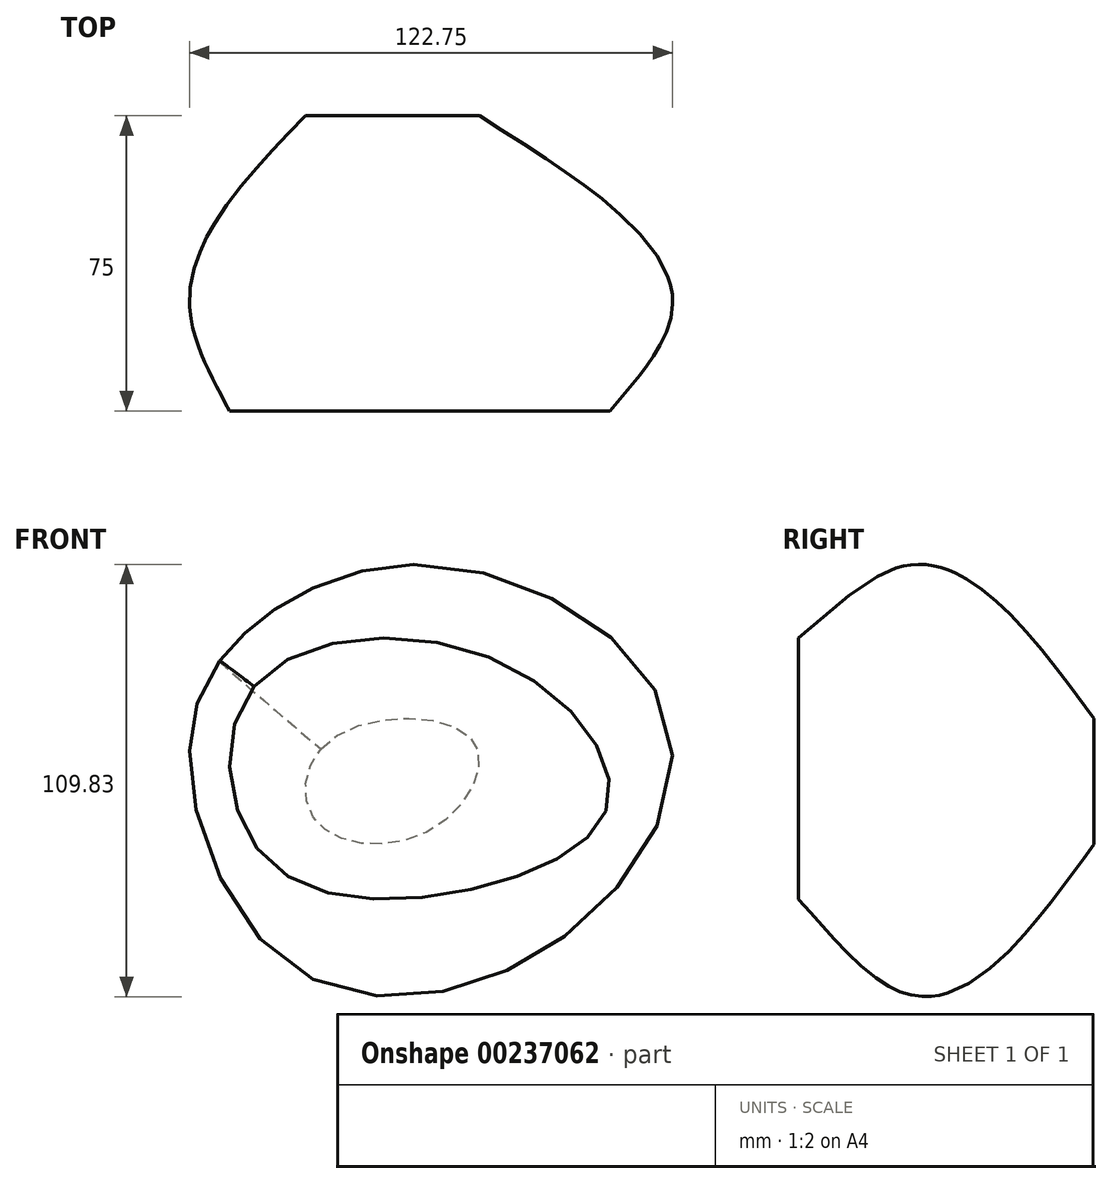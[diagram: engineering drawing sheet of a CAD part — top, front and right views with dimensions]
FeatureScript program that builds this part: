
annotation { "Feature Type Name" : "Feature", "Feature Type Description" : "" }
export const myFeature = defineFeature(function(context is Context, id is Id, definition is map)
    precondition{}
    {
        {
            var Q0;
            Q0=qCreatedBy(makeId("Front.planeOp"),FACE);
            var sketch = newSketch(context, id + "F0", { "sketchPlane" : qUnion([Q0])});
            skFitSpline(sketch, "E0", {"points": [v(-29.58, 23.58) * mm, v(32.51, 30.02) * mm, v(60.63, -5.13) * mm, v(29, -27.1) * mm, v(-26.07, -20.65) * mm, v(-29.58, 23.58) * mm]});
            skSolve(sketch);
        }
        {
            var Q0;
            Q0=qCreatedBy(makeId("Front.planeOp"),FACE);
            cPlane(context, id + "F1", {"entities" : qUnion([Q0]), "cplaneType" : CPlaneType.OFFSET, "offset" : 25 * mm, "oppositeDirection" : true, "width" : 150 * mm, "height" : 150 * mm});
        }
        {
            var Q0;
            Q0=qCreatedBy(id+"F1.planeOp",FACE);
            var sketch = newSketch(context, id + "F2", { "sketchPlane" : qUnion([Q0])});
            skFitSpline(sketch, "E1", {"points": [v(-33.39, 35.59) * mm, v(18.16, 53.45) * mm, v(75.27, 14.5) * mm, v(48.62, -39.69) * mm, v(-17.28, -47.89) * mm, v(-45.7, 2.78) * mm, v(-33.39, 35.59) * mm]});
            skSolve(sketch);
        }
        {
            var Q0;
            Q0=qCreatedBy(id+"F1.planeOp",FACE);
            cPlane(context, id + "F3", {"entities" : qUnion([Q0]), "cplaneType" : CPlaneType.OFFSET, "offset" : 50 * mm, "oppositeDirection" : true, "width" : 150 * mm, "height" : 150 * mm});
        }
        {
            var Q0;
            Q0=qCreatedBy(id+"F3.planeOp",FACE);
            var sketch = newSketch(context, id + "F4", { "sketchPlane" : qUnion([Q0])});
            skFitSpline(sketch, "E2", {"points": [v(-9.67, 10.4) * mm, v(26.07, 9.81) * mm, v(15.52, -12.74) * mm, v(-13.77, -10.7) * mm, v(-9.67, 10.4) * mm]});
            skSolve(sketch);
        }
        {
            var Q0;
            Q0=makeQuery(id+"F0.imprint","IMPRINT",FACE,{"disambiguationData":[TD([[makeQuery(id+"F0.imprint","IMPRINT",EDGE,{"derivedFrom":sQuery(id+"F0.wireOp",EDGE,"E0")}),-1.0]])]});
            var Q1;
            Q1=makeQuery(id+"F2.imprint","IMPRINT",FACE,{"disambiguationData":[TD([[makeQuery(id+"F2.imprint","IMPRINT",EDGE,{"derivedFrom":sQuery(id+"F2.wireOp",EDGE,"E1")}),-1.0]])]});
            var Q2;
            Q2=makeQuery(id+"F4.imprint","IMPRINT",FACE,{"disambiguationData":[TD([[makeQuery(id+"F4.imprint","IMPRINT",EDGE,{"derivedFrom":sQuery(id+"F4.wireOp",EDGE,"E2")}),-1.0]])]});
            loft(context, id + "F5", {"sheetProfilesArray" : [{ "sheetProfileEntities" : qUnion([Q0]) }, { "sheetProfileEntities" : qUnion([Q1]) }, { "sheetProfileEntities" : qUnion([Q2]) }]});
        }
    });
